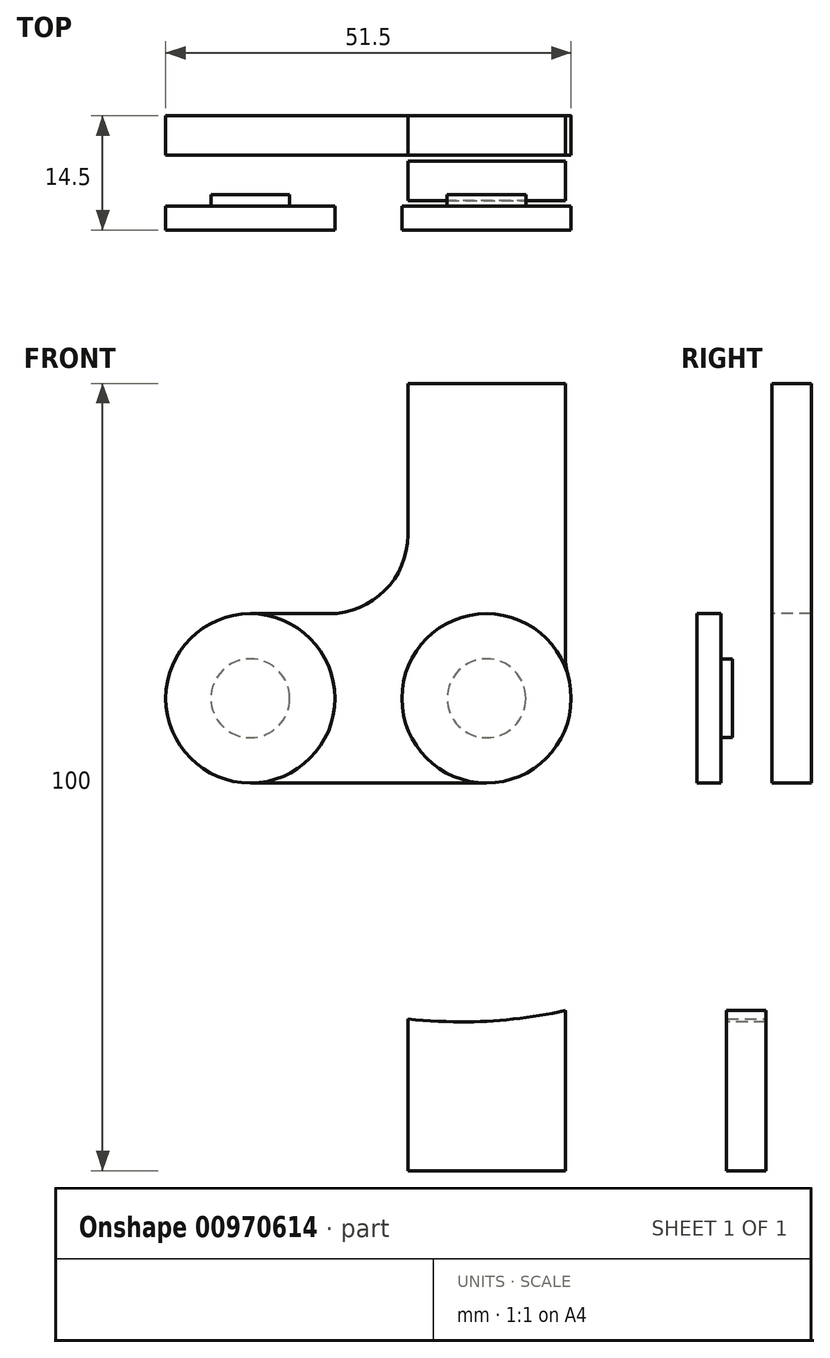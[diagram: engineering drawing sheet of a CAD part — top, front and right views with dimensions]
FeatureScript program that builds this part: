
annotation { "Feature Type Name" : "Feature", "Feature Type Description" : "" }
export const myFeature = defineFeature(function(context is Context, id is Id, definition is map)
    precondition{}
    {
        {
            assignVariable(context, id + "F0", {"name" : "Tbrace", "anyValue" : 5});
        }
        {
            assignVariable(context, id + "F1", {"name" : "Zclearance", "anyValue" : 0.75});
        }
        {
            assignVariable(context, id + "F2", {"name" : "Hpin", "anyValue" : getVariable(context, 'Tbrace') + 2 * getVariable(context, 'Zclearance')});
        }
        {
            assignVariable(context, id + "F3", {"name" : "Tcap", "anyValue" : 3});
        }
        {
            var Q0;
            Q0=qCreatedBy(makeId("Front.planeOp"),FACE);
            var sketch = newSketch(context, id + "F4", { "sketchPlane" : qUnion([Q0])});
            skCircle(sketch, "E0", {"center": v(0, 0) * mm, "radius": 5 * mm});
            skCircle(sketch, "E1", {"center": v(-30, 0) * mm, "radius": 5 * mm});
            skLineSegment(sketch, "E2", {"start": v(0, 0) * mm, "end": v(-30, 0) * mm, "construction": true});
            skSolve(sketch);
        }
        {
            var Q0;
            Q0=qCreatedBy(makeId("Front.planeOp"),FACE);
            var sketch = newSketch(context, id + "F5", { "sketchPlane" : qUnion([Q0])});
            skArc(sketch, "E3", {"start": v(0, 0) * mm, "mid": v(4.76, 8.78) * mm, "end": v(7.87, 18.27) * mm, "construction": true});
            skLineSegment(sketch, "E4", {"start": v(-46.2, 30.74) * mm, "end": v(0, 0) * mm, "construction": true});
            skLineSegment(sketch, "E5", {"start": v(-46.2, 30.74) * mm, "end": v(7.87, 18.27) * mm, "construction": true});
            skArc(sketch, "E6.0.startCap", {"start": v(4.79, -3.19) * mm, "mid": v(-3.19, -4.79) * mm, "end": v(-4.79, 3.19) * mm});
            skArc(sketch, "E6.0.endCap", {"start": v(2.27, 19.56) * mm, "mid": v(9.17, 23.87) * mm, "end": v(13.48, 16.98) * mm});
            skArc(sketch, "E6.0.left", {"start": v(-4.79, 3.19) * mm, "mid": v(-0.52, 11.05) * mm, "end": v(2.27, 19.56) * mm});
            skArc(sketch, "E6.0.right", {"start": v(4.79, -3.19) * mm, "mid": v(10.04, 6.5) * mm, "end": v(13.48, 16.98) * mm});
            skPoint(sketch, "E7", {"position": v(25.08, -6.3) * mm});
            skLineSegment(sketch, "E8", {"start": v(7.87, 18.27) * mm, "end": v(25.08, -6.3) * mm, "construction": true});
            skLineSegment(sketch, "E9.1.0", {"start": v(-46.2, 30.74) * mm, "end": v(1.08, 1.68) * mm, "construction": true});
            skLineSegment(sketch, "E9.2.0", {"start": v(-46.2, 30.74) * mm, "end": v(2.1, 3.4) * mm, "construction": true});
            skLineSegment(sketch, "E9.3.0", {"start": v(-46.2, 30.74) * mm, "end": v(3.05, 5.17) * mm, "construction": true});
            skLineSegment(sketch, "E9.4.0", {"start": v(-46.2, 30.74) * mm, "end": v(3.94, 6.96) * mm, "construction": true});
            skLineSegment(sketch, "E9.5.0", {"start": v(-46.2, 30.74) * mm, "end": v(4.76, 8.78) * mm, "construction": true});
            skLineSegment(sketch, "E9.6.0", {"start": v(-46.2, 30.74) * mm, "end": v(5.52, 10.63) * mm, "construction": true});
            skLineSegment(sketch, "E9.7.0", {"start": v(-46.2, 30.74) * mm, "end": v(6.21, 12.5) * mm, "construction": true});
            skLineSegment(sketch, "E9.8.0", {"start": v(-46.2, 30.74) * mm, "end": v(6.84, 14.4) * mm, "construction": true});
            skLineSegment(sketch, "E9.9.0", {"start": v(-46.2, 30.74) * mm, "end": v(7.39, 16.33) * mm, "construction": true});
            skLineSegment(sketch, "E10", {"start": v(7.39, 16.33) * mm, "end": v(18.87, -11.39) * mm, "construction": true});
            skLineSegment(sketch, "E11", {"start": v(6.84, 14.4) * mm, "end": v(12.04, -15.14) * mm, "construction": true});
            skLineSegment(sketch, "E12", {"start": v(6.21, 12.5) * mm, "end": v(4.9, -17.47) * mm, "construction": true});
            skLineSegment(sketch, "E13", {"start": v(5.52, 10.63) * mm, "end": v(-2.24, -18.35) * mm, "construction": true});
            skLineSegment(sketch, "E14", {"start": v(4.76, 8.78) * mm, "end": v(-9.1, -17.83) * mm, "construction": true});
            skLineSegment(sketch, "E15", {"start": v(3.94, 6.96) * mm, "end": v(-15.35, -16.02) * mm, "construction": true});
            skLineSegment(sketch, "E16", {"start": v(3.05, 5.17) * mm, "end": v(-20.75, -13.1) * mm, "construction": true});
            skLineSegment(sketch, "E17", {"start": v(2.1, 3.4) * mm, "end": v(-25.1, -9.27) * mm, "construction": true});
            skLineSegment(sketch, "E18", {"start": v(1.08, 1.68) * mm, "end": v(-28.21, -4.8) * mm, "construction": true});
            skLineSegment(sketch, "E19", {"start": v(0, 0) * mm, "end": v(-30, 0) * mm, "construction": true});
            skFitSpline(sketch, "E20", {"points": [v(-30, 0) * mm, v(-28.21, -4.8) * mm, v(-25.1, -9.27) * mm, v(-20.75, -13.1) * mm, v(-15.35, -16.02) * mm, v(-9.1, -17.83) * mm, v(-2.24, -18.35) * mm, v(4.9, -17.47) * mm, v(12.04, -15.14) * mm, v(18.87, -11.39) * mm, v(25.08, -6.3) * mm], "startDerivative": vector(0, -79.8) * mm, "endDerivative": vector(58.16, 58.67) * mm, "construction": true});
            skLineSegment(sketch, "E21.0.startCap", {"start": v(-35.75, 0) * mm, "end": v(-35.75, 0) * mm});
            skLineSegment(sketch, "E21.0.endCap", {"start": v(29.16, -10.35) * mm, "end": v(29.16, -10.35) * mm});
            skFitSpline(sketch, "E21.0.left", {"points": [v(-35.75, 0) * mm, v(-35.75, -0.67) * mm, v(-35.66, -1.99) * mm, v(-35.23, -3.85) * mm, v(-34.69, -5.2) * mm, v(-34.22, -6.1) * mm, v(-33.87, -6.68) * mm, v(-33.55, -7.18) * mm, v(-33.27, -7.6) * mm, v(-33.07, -7.89) * mm, v(-32.93, -8.1) * mm, v(-32.8, -8.3) * mm, v(-32.6, -8.59) * mm, v(-32.28, -9.08) * mm, v(-31.85, -9.75) * mm, v(-31.27, -10.62) * mm, v(-30.61, -11.56) * mm, v(-30, -12.36) * mm, v(-29.45, -13.03) * mm, v(-28.89, -13.68) * mm, v(-28.16, -14.44) * mm, v(-27.25, -15.3) * mm, v(-26.33, -16.1) * mm, v(-25.38, -16.86) * mm, v(-24.42, -17.56) * mm, v(-23.14, -18.43) * mm, v(-21.46, -19.46) * mm, v(-19.69, -20.39) * mm, v(-18.22, -21.06) * mm, v(-16.72, -21.68) * mm, v(-14.81, -22.36) * mm, v(-11.68, -23.24) * mm, v(-7.66, -23.95) * mm, v(-3.54, -24.17) * mm, v(-0.23, -24.03) * mm, v(2.25, -23.79) * mm, v(4.71, -23.4) * mm, v(7.15, -22.87) * mm, v(9.58, -22.2) * mm, v(11.58, -21.52) * mm, v(13.17, -20.9) * mm, v(14.36, -20.4) * mm, v(15.53, -19.87) * mm, v(17.07, -19.12) * mm, v(18.94, -18.12) * mm, v(20.72, -17.04) * mm, v(22.1, -16.15) * mm, v(23.44, -15.24) * mm, v(25.12, -14) * mm, v(27.13, -12.32) * mm, v(28.48, -11.04) * mm, v(29.16, -10.35) * mm]});
            skFitSpline(sketch, "E21.0.right", {"points": [v(-35.75, 0) * mm, v(-35.75, -0.67) * mm, v(-35.66, -1.99) * mm, v(-35.23, -3.85) * mm, v(-34.69, -5.2) * mm, v(-34.22, -6.1) * mm, v(-33.87, -6.68) * mm, v(-33.55, -7.18) * mm, v(-33.27, -7.6) * mm, v(-33.07, -7.89) * mm, v(-32.93, -8.1) * mm, v(-32.8, -8.3) * mm, v(-32.6, -8.59) * mm, v(-32.28, -9.08) * mm, v(-31.85, -9.75) * mm, v(-31.27, -10.62) * mm, v(-30.61, -11.56) * mm, v(-30, -12.36) * mm, v(-29.45, -13.03) * mm, v(-28.89, -13.68) * mm, v(-28.16, -14.44) * mm, v(-27.25, -15.3) * mm, v(-26.33, -16.1) * mm, v(-25.38, -16.86) * mm, v(-24.42, -17.56) * mm, v(-23.14, -18.43) * mm, v(-21.46, -19.46) * mm, v(-19.69, -20.39) * mm, v(-18.22, -21.06) * mm, v(-16.72, -21.68) * mm, v(-14.81, -22.36) * mm, v(-11.68, -23.24) * mm, v(-7.66, -23.95) * mm, v(-3.54, -24.17) * mm, v(-0.23, -24.03) * mm, v(2.25, -23.79) * mm, v(4.71, -23.4) * mm, v(7.15, -22.87) * mm, v(9.58, -22.2) * mm, v(11.58, -21.52) * mm, v(13.17, -20.9) * mm, v(14.36, -20.4) * mm, v(15.53, -19.87) * mm, v(17.07, -19.12) * mm, v(18.94, -18.12) * mm, v(20.72, -17.04) * mm, v(22.1, -16.15) * mm, v(23.44, -15.24) * mm, v(25.12, -14) * mm, v(27.13, -12.32) * mm, v(28.48, -11.04) * mm, v(29.16, -10.35) * mm]});
            skArc(sketch, "E22", {"start": v(-35.75, 0) * mm, "mid": v(-30, 5.75) * mm, "end": v(-24.25, 0) * mm});
            skArc(sketch, "E23", {"start": v(29.16, -10.35) * mm, "mid": v(29.13, -2.22) * mm, "end": v(21, -2.26) * mm});
            skLineSegment(sketch, "E24", {"start": v(25.08, -6.3) * mm, "end": v(22.94, -8.46) * mm, "construction": true});
            skFitSpline(sketch, "E25.0", {"points": [v(-24.25, 0) * mm, v(-24.25, -0.16) * mm, v(-24.23, -0.35) * mm, v(-24.22, -0.39) * mm, v(-24.21, -0.4) * mm, v(-24.16, -0.5) * mm, v(-24.08, -0.64) * mm, v(-23.96, -0.84) * mm, v(-23.77, -1.11) * mm, v(-23.57, -1.4) * mm, v(-23.38, -1.68) * mm, v(-23.2, -1.96) * mm, v(-22.98, -2.3) * mm, v(-22.64, -2.82) * mm, v(-22.23, -3.44) * mm, v(-21.76, -4.15) * mm, v(-21.31, -4.79) * mm, v(-20.95, -5.26) * mm, v(-20.68, -5.6) * mm, v(-20.4, -5.91) * mm, v(-20.02, -6.31) * mm, v(-19.53, -6.78) * mm, v(-19, -7.24) * mm, v(-18.42, -7.7) * mm, v(-17.8, -8.15) * mm, v(-16.92, -8.75) * mm, v(-15.78, -9.45) * mm, v(-14.6, -10.07) * mm, v(-13.62, -10.52) * mm, v(-12.62, -10.93) * mm, v(-11.34, -11.39) * mm, v(-9.19, -12) * mm, v(-6.36, -12.5) * mm, v(-3.42, -12.65) * mm, v(-1.04, -12.55) * mm, v(1.38, -12.31) * mm, v(4.42, -11.74) * mm, v(7.1, -10.93) * mm, v(8.86, -10.24) * mm, v(9.74, -9.88) * mm, v(10.61, -9.48) * mm, v(11.78, -8.9) * mm, v(13.24, -8.12) * mm, v(14.65, -7.27) * mm, v(15.75, -6.56) * mm, v(16.54, -6.03) * mm, v(17.29, -5.49) * mm, v(18.26, -4.75) * mm, v(19.46, -3.75) * mm, v(20.47, -2.8) * mm, v(21, -2.26) * mm]});
            skSolve(sketch);
        }
        {
            var Q0;
            Q0=qCreatedBy(makeId("Front.planeOp"),FACE);
            var sketch = newSketch(context, id + "F6", { "sketchPlane" : qUnion([Q0])});
            skArc(sketch, "E26", {"start": v(-30, 10.75) * mm, "mid": v(-40.75, 0) * mm, "end": v(-30, -10.75) * mm});
            skArc(sketch, "E27", {"start": v(0, -10.75) * mm, "mid": v(8.55, -6.51) * mm, "end": v(10.36, 2.86) * mm});
            skLineSegment(sketch, "E28", {"start": v(-30, -10.75) * mm, "end": v(0, -10.75) * mm});
            skLineSegment(sketch, "E29", {"start": v(-30, 10.75) * mm, "end": v(-20, 10.75) * mm});
            skLineSegment(sketch, "E30", {"start": v(-10, 20.75) * mm, "end": v(-10, 40) * mm});
            skLineSegment(sketch, "E31", {"start": v(10, 5.53) * mm, "end": v(10, 40) * mm});
            skLineSegment(sketch, "E32", {"start": v(10, 40) * mm, "end": v(-10, 40) * mm});
            skPoint(sketch, "E33", {"position": v(0, 40) * mm});
            skPoint(sketch, "E34.visualSharp", {"position": v(10, 3.94) * mm});
            skArc(sketch, "E34.filletArc", {"start": v(10, 5.53) * mm, "mid": v(10.1, 4.18) * mm, "end": v(10.36, 2.86) * mm});
            skPoint(sketch, "E35.visualSharp", {"position": v(-10, 10.75) * mm});
            skArc(sketch, "E35.filletArc", {"start": v(-20, 10.75) * mm, "mid": v(-12.93, 13.68) * mm, "end": v(-10, 20.75) * mm});
            skSolve(sketch);
        }
        {
            var Q0;
            Q0=qCreatedBy(makeId("Front.planeOp"),FACE);
            var sketch = newSketch(context, id + "F7", { "sketchPlane" : qUnion([Q0])});
            skArc(sketch, "E36", {"start": v(-34.67, 9.68) * mm, "mid": v(-39.1, 5.72) * mm, "end": v(-40.75, 0) * mm});
            skArc(sketch, "E37", {"start": v(32.72, -13.87) * mm, "mid": v(35.8, -7.22) * mm, "end": v(33.89, -0.14) * mm});
            skArc(sketch, "E38", {"start": v(16.68, 24.43) * mm, "mid": v(10.59, 28.67) * mm, "end": v(3.2, 27.95) * mm});
            skFitSpline(sketch, "E39.0", {"points": [v(-53, 0) * mm, v(-53, -1) * mm, v(-52.86, -2.92) * mm, v(-52.38, -5.5) * mm, v(-51.72, -7.76) * mm, v(-51.12, -9.39) * mm, v(-50.63, -10.56) * mm, v(-50.27, -11.37) * mm, v(-49.98, -12) * mm, v(-49.76, -12.47) * mm, v(-49.54, -12.92) * mm, v(-49.26, -13.5) * mm, v(-48.79, -14.44) * mm, v(-48.16, -15.63) * mm, v(-47.34, -17.08) * mm, v(-46.45, -18.57) * mm, v(-45.62, -19.81) * mm, v(-44.92, -20.81) * mm, v(-44.18, -21.81) * mm, v(-43.22, -23.02) * mm, v(-42.01, -24.42) * mm, v(-40.76, -25.74) * mm, v(-39.47, -27.01) * mm, v(-38.14, -28.22) * mm, v(-36.78, -29.38) * mm, v(-35.37, -30.48) * mm, v(-33.45, -31.88) * mm, v(-30.95, -33.5) * mm, v(-27.8, -35.25) * mm, v(-24.54, -36.77) * mm, v(-21.18, -38.06) * mm, v(-17.74, -39.12) * mm, v(-13.06, -40.23) * mm, v(-8.29, -40.89) * mm, v(-3.48, -41.08) * mm, v(0.14, -41) * mm, v(3.75, -40.71) * mm, v(7.36, -40.19) * mm, v(10.93, -39.45) * mm, v(14.43, -38.5) * mm, v(17.87, -37.37) * mm, v(21.23, -36.04) * mm, v(24.52, -34.5) * mm, v(27.74, -32.78) * mm, v(30.9, -30.87) * mm, v(34.04, -28.73) * mm, v(37.1, -26.39) * mm, v(39.05, -24.65) * mm, v(40, -23.69) * mm]});
            skLineSegment(sketch, "E40", {"start": v(-34.67, 9.68) * mm, "end": v(3.2, 27.95) * mm});
            skLineSegment(sketch, "E41", {"start": v(16.68, 24.43) * mm, "end": v(33.89, -0.14) * mm});
            skLineSegment(sketch, "E42", {"start": v(-10, -36.42) * mm, "end": v(-10, -60) * mm});
            skLineSegment(sketch, "E43", {"start": v(10, -34.3) * mm, "end": v(10, -60) * mm});
            skLineSegment(sketch, "E44", {"start": v(10, -60) * mm, "end": v(-10, -60) * mm});
            skPoint(sketch, "E45", {"position": v(0, -60) * mm});
            skFitSpline(sketch, "E46.trimOffspring", {"points": [v(-53, 0) * mm, v(-53, -1) * mm, v(-52.86, -2.92) * mm, v(-52.38, -5.5) * mm, v(-51.72, -7.76) * mm, v(-51.12, -9.39) * mm, v(-50.63, -10.56) * mm, v(-50.27, -11.37) * mm, v(-49.98, -12) * mm, v(-49.76, -12.47) * mm, v(-49.54, -12.92) * mm, v(-49.26, -13.5) * mm, v(-48.79, -14.44) * mm, v(-48.16, -15.63) * mm, v(-47.34, -17.08) * mm, v(-46.45, -18.57) * mm, v(-45.62, -19.81) * mm, v(-44.92, -20.81) * mm, v(-44.18, -21.81) * mm, v(-43.22, -23.02) * mm, v(-42.01, -24.42) * mm, v(-40.76, -25.74) * mm, v(-39.47, -27.01) * mm, v(-38.14, -28.22) * mm, v(-36.78, -29.38) * mm, v(-35.37, -30.48) * mm, v(-33.45, -31.88) * mm, v(-30.95, -33.5) * mm, v(-27.8, -35.25) * mm, v(-24.54, -36.77) * mm, v(-21.18, -38.06) * mm, v(-17.74, -39.12) * mm, v(-13.06, -40.23) * mm, v(-8.29, -40.89) * mm, v(-3.48, -41.08) * mm, v(0.14, -41) * mm, v(3.75, -40.71) * mm, v(7.36, -40.19) * mm, v(10.93, -39.45) * mm, v(14.43, -38.5) * mm, v(17.87, -37.37) * mm, v(21.23, -36.04) * mm, v(24.52, -34.5) * mm, v(27.74, -32.78) * mm, v(30.9, -30.87) * mm, v(34.04, -28.73) * mm, v(37.1, -26.39) * mm, v(39.05, -24.65) * mm, v(40, -23.69) * mm]});
            skPoint(sketch, "E47.visualSharp", {"position": v(-10, -28.58) * mm});
            skArc(sketch, "E47.filletArc", {"start": v(-10, -36.42) * mm, "mid": v(-11.9, -30.57) * mm, "end": v(-16.85, -26.93) * mm});
            skPoint(sketch, "E48.visualSharp", {"position": v(10, -27.26) * mm});
            skArc(sketch, "E48.filletArc", {"start": v(16.05, -25.12) * mm, "mid": v(11.65, -28.8) * mm, "end": v(10, -34.3) * mm});
            skSolve(sketch);
        }
        {
            var Q0;
            Q0=qSketchRegion(id+"F6",true);
            extrude(context, id + "F8", {"entities" : qUnion([Q0]), "oppositeDirection" : true, "depth" : (getVariable(context, 'Tbrace')) * mm, "offsetDistance" : 25 * mm});
        }
        {
            var Q0;
            Q0=qSketchRegion(id+"F4",true);
            extrude(context, id + "F9", {"entities" : qUnion([Q0]), "operationType" : NewBodyOperationType.ADD, "depth" : (getVariable(context, 'Hpin')) * mm, "offsetDistance" : 25 * mm});
        }
        {
            var Q0;
            Q0=qSketchRegion(id+"F7",true);
            extrude(context, id + "F10", {"entities" : qUnion([Q0]), "depth" : (getVariable(context, 'Tbrace')) * mm, "offsetDistance" : 25 * mm});
        }
        {
            var Q0;
            Q0=qSketchRegion(id+"F5",true);
            var Q1;
            Q1=makeQuery(id+"F10.opExtrude","CAP_FACE",FACE,{"disambiguationData":[OSD([sQuery(id+"F7.wireOp",EDGE,"E36"),sQuery(id+"F7.wireOp",EDGE,"E37"),sQuery(id+"F7.wireOp",EDGE,"E38"),sQuery(id+"F7.wireOp",EDGE,"E39.0"),sQuery(id+"F7.wireOp",EDGE,"E40"),sQuery(id+"F7.wireOp",EDGE,"E41"),sQuery(id+"F7.wireOp",EDGE,"E42"),sQuery(id+"F7.wireOp",EDGE,"E43"),sQuery(id+"F7.wireOp",EDGE,"E44"),sQuery(id+"F7.wireOp",EDGE,"E46.trimOffspring"),sQuery(id+"F7.wireOp",EDGE,"E47.filletArc"),sQuery(id+"F7.wireOp",EDGE,"E48.filletArc")])],"isStart":false});
            extrude(context, id + "F11", {"entities" : qUnion([Q0]), "operationType" : NewBodyOperationType.REMOVE, "endBound" : BoundingType.UP_TO_SURFACE, "depth" : 25 * mm, "endBoundEntityFace" : qUnion([Q1]), "offsetDistance" : 25 * mm});
        }
        {
            var Q0;
            Q0=makeQuery(id+"F10.opExtrude","SWEPT_BODY",BODY,{"disambiguationData":[OSD([sQuery(id+"F7.wireOp",EDGE,"E36"),sQuery(id+"F7.wireOp",EDGE,"E37"),sQuery(id+"F7.wireOp",EDGE,"E38"),sQuery(id+"F7.wireOp",EDGE,"E39.0"),sQuery(id+"F7.wireOp",EDGE,"E40"),sQuery(id+"F7.wireOp",EDGE,"E41"),sQuery(id+"F7.wireOp",EDGE,"E42"),sQuery(id+"F7.wireOp",EDGE,"E43"),sQuery(id+"F7.wireOp",EDGE,"E44"),sQuery(id+"F7.wireOp",EDGE,"E46.trimOffspring"),sQuery(id+"F7.wireOp",EDGE,"E47.filletArc"),sQuery(id+"F7.wireOp",EDGE,"E48.filletArc")])]});
            transform(context, id + "F12", {"entities" : qUnion([Q0]), "transformType" : TransformType.TRANSLATION_3D, "dx" : 0 * mm, "dy" : (-getVariable(context, 'Zclearance')) * mm, "dz" : 0 * mm, "makeCopy" : false});
        }
        {
            var Q0;
            Q0=makeQuery(id+"F9.opExtrude","CAP_FACE",FACE,{"disambiguationData":[OSD([sQuery(id+"F4.wireOp",EDGE,"E0")])],"isStart":false});
            var sketch = newSketch(context, id + "F13", { "sketchPlane" : qUnion([Q0])});
            skCircle(sketch, "E49", {"center": v(0, 0) * mm, "radius": 10.75 * mm});
            skCircle(sketch, "E50", {"center": v(-30, 0) * mm, "radius": 10.75 * mm});
            skSolve(sketch);
        }
        {
            var Q0;
            Q0=qSketchRegion(id+"F13",true);
            extrude(context, id + "F14", {"entities" : qUnion([Q0]), "operationType" : NewBodyOperationType.ADD, "depth" : (getVariable(context, 'Tcap')) * mm, "offsetDistance" : 25 * mm});
        }
    });
